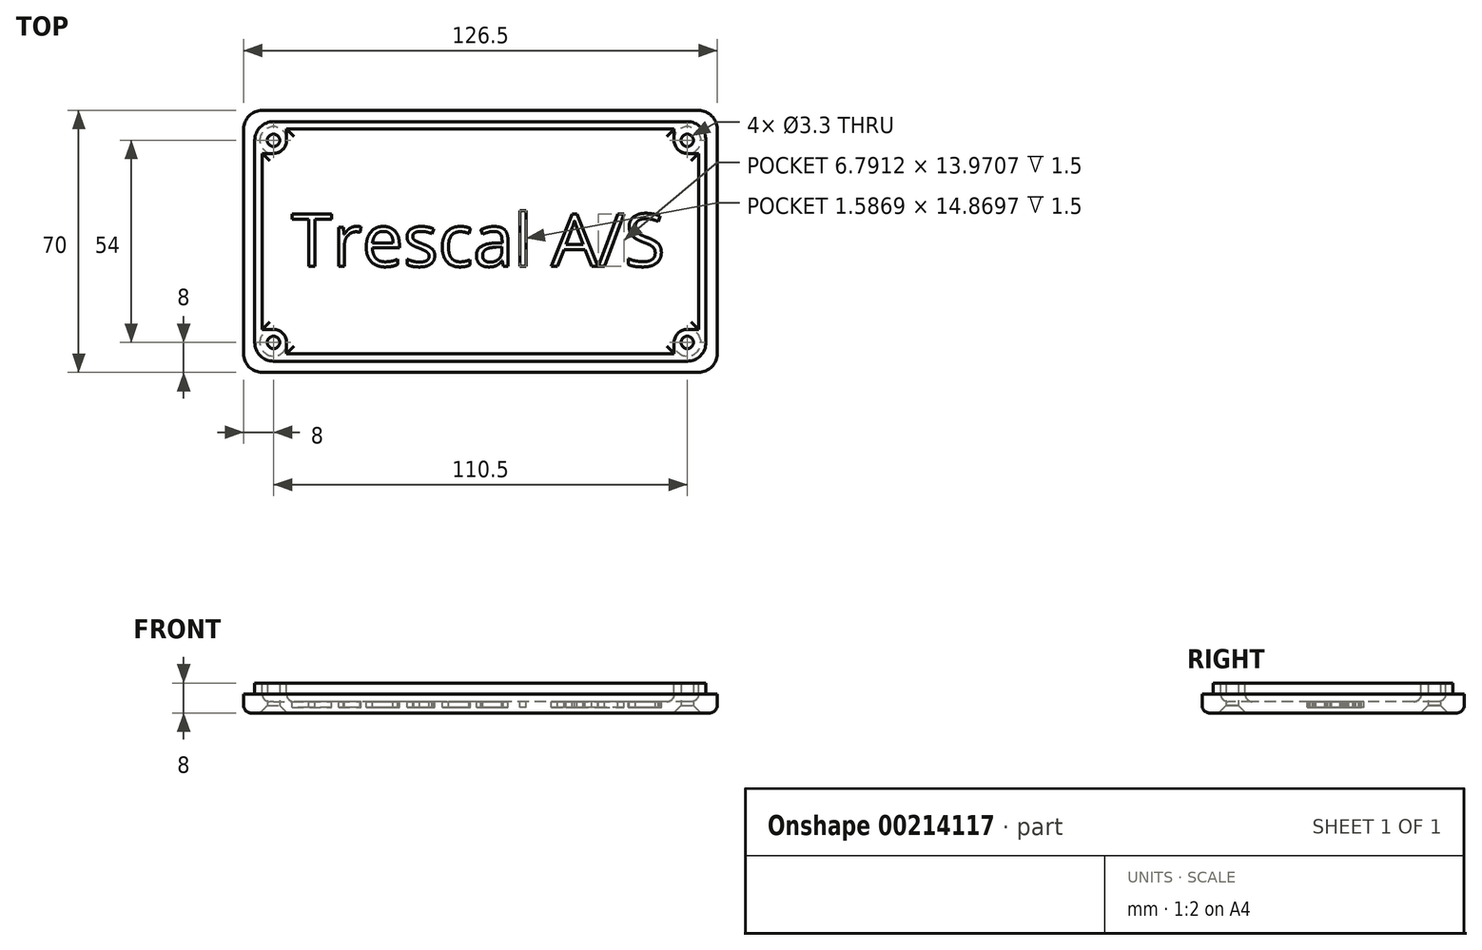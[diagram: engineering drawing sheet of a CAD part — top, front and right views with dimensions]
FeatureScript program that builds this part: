
annotation { "Feature Type Name" : "Feature", "Feature Type Description" : "" }
export const myFeature = defineFeature(function(context is Context, id is Id, definition is map)
    precondition{}
    {
        {
            var Q0;
            Q0=qCreatedBy(makeId("Top.planeOp"),FACE);
            var sketch = newSketch(context, id + "F0", { "sketchPlane" : qUnion([Q0])});
            skLineSegment(sketch, "E0.bottom", {"start": v(58.25, -35) * mm, "end": v(-58.25, -35) * mm});
            skLineSegment(sketch, "E0.top", {"start": v(58.25, 35) * mm, "end": v(-58.25, 35) * mm});
            skLineSegment(sketch, "E0.left", {"start": v(63.25, -30) * mm, "end": v(63.25, 30) * mm});
            skLineSegment(sketch, "E0.right", {"start": v(-63.25, -30) * mm, "end": v(-63.25, 30) * mm});
            skPoint(sketch, "E0.middle", {"position": v(0, 0) * mm});
            skPoint(sketch, "E1.visualSharp", {"position": v(-63.25, 35) * mm});
            skArc(sketch, "E1.filletArc", {"start": v(-58.25, 35) * mm, "mid": v(-61.79, 33.54) * mm, "end": v(-63.25, 30) * mm});
            skPoint(sketch, "E2.visualSharp", {"position": v(63.25, 35) * mm});
            skArc(sketch, "E2.filletArc", {"start": v(63.25, 30) * mm, "mid": v(61.79, 33.54) * mm, "end": v(58.25, 35) * mm});
            skPoint(sketch, "E3.visualSharp", {"position": v(63.25, -35) * mm});
            skArc(sketch, "E3.filletArc", {"start": v(58.25, -35) * mm, "mid": v(61.79, -33.54) * mm, "end": v(63.25, -30) * mm});
            skPoint(sketch, "E4.visualSharp", {"position": v(-63.25, -35) * mm});
            skArc(sketch, "E4.filletArc", {"start": v(-63.25, -30) * mm, "mid": v(-61.79, -33.54) * mm, "end": v(-58.25, -35) * mm});
            skLineSegment(sketch, "E5.bottom", {"start": v(55.25, -32) * mm, "end": v(-55.25, -32) * mm});
            skLineSegment(sketch, "E5.top", {"start": v(55.25, 32) * mm, "end": v(-55.25, 32) * mm});
            skLineSegment(sketch, "E5.left", {"start": v(60.25, -27) * mm, "end": v(60.25, 27) * mm});
            skLineSegment(sketch, "E5.right", {"start": v(-60.25, -27) * mm, "end": v(-60.25, 27) * mm});
            skPoint(sketch, "E6.visualSharp", {"position": v(-60.25, 32) * mm});
            skArc(sketch, "E6.filletArc", {"start": v(-55.25, 32) * mm, "mid": v(-58.79, 30.54) * mm, "end": v(-60.25, 27) * mm});
            skPoint(sketch, "E7.visualSharp", {"position": v(60.25, 32) * mm});
            skArc(sketch, "E7.filletArc", {"start": v(60.25, 27) * mm, "mid": v(58.79, 30.54) * mm, "end": v(55.25, 32) * mm});
            skPoint(sketch, "E8.visualSharp", {"position": v(60.25, -32) * mm});
            skArc(sketch, "E8.filletArc", {"start": v(55.25, -32) * mm, "mid": v(58.79, -30.54) * mm, "end": v(60.25, -27) * mm});
            skPoint(sketch, "E9.visualSharp", {"position": v(-60.25, -32) * mm});
            skArc(sketch, "E9.filletArc", {"start": v(-60.25, -27) * mm, "mid": v(-58.79, -30.54) * mm, "end": v(-55.25, -32) * mm});
            skSolve(sketch);
        }
        {
            var Q0;
            Q0=makeQuery(id+"F0.imprint","IMPRINT",FACE,{"disambiguationData":[TD([[makeQuery(id+"F0.imprint","IMPRINT",EDGE,{"derivedFrom":sQuery(id+"F0.wireOp",EDGE,"E5.bottom")}),-1.0]])]});
            extrude(context, id + "F1", {"entities" : qUnion([Q0]), "depth" : 8 * mm});
        }
        {
            var Q0;
            Q0 = qSketchRegion(id + "F0", true);
            extrude(context, id + "F2", {"entities" : qUnion([Q0]), "operationType" : NewBodyOperationType.ADD, "depth" : 5 * mm});
        }
        {
            var Q0;
            Q0=sQuery(id+"F0.wireOp",VERTEX,"E9.filletArc.center");
            var Q1;
            Q1=sQuery(id+"F0.wireOp",VERTEX,"E8.filletArc.center");
            var Q2;
            Q2=sQuery(id+"F0.wireOp",VERTEX,"E7.filletArc.center");
            var Q3;
            Q3=sQuery(id+"F0.wireOp",VERTEX,"E6.filletArc.center");
            var Q4;
            Q4=makeQuery(id+"F1.opExtrude","SWEPT_BODY",BODY,{"disambiguationData":[OSD([sQuery(id+"F0.wireOp",EDGE,"E5.bottom"),sQuery(id+"F0.wireOp",EDGE,"E5.top"),sQuery(id+"F0.wireOp",EDGE,"E5.left"),sQuery(id+"F0.wireOp",EDGE,"E5.right"),sQuery(id+"F0.wireOp",EDGE,"E6.filletArc"),sQuery(id+"F0.wireOp",EDGE,"E7.filletArc"),sQuery(id+"F0.wireOp",EDGE,"E8.filletArc"),sQuery(id+"F0.wireOp",EDGE,"E9.filletArc")])]});
            hole(context, id + "F3", {"style" : HoleStyle.C_SINK, "endStyle" : HoleEndStyle.THROUGH, "oppositeDirection" : true, "holeDiameter" : 3.3 * mm, "cSinkDiameter" : 7.3 * mm, "cSinkAngle" : 90 * degree, "locations" : qUnion([Q0, Q1, Q2, Q3]), "scope" : qUnion([Q4]), "isTappedThrough" : true});
        }
        {
            var Q0;
            Q0=makeQuery(id+"F1.opExtrude","CAP_FACE",FACE,{"disambiguationData":[OSD([sQuery(id+"F0.wireOp",EDGE,"E5.bottom"),sQuery(id+"F0.wireOp",EDGE,"E5.top"),sQuery(id+"F0.wireOp",EDGE,"E5.left"),sQuery(id+"F0.wireOp",EDGE,"E5.right"),sQuery(id+"F0.wireOp",EDGE,"E6.filletArc"),sQuery(id+"F0.wireOp",EDGE,"E7.filletArc"),sQuery(id+"F0.wireOp",EDGE,"E8.filletArc"),sQuery(id+"F0.wireOp",EDGE,"E9.filletArc")])],"isStart":false});
            var sketch = newSketch(context, id + "F4", { "sketchPlane" : qUnion([Q0])});
            skLineSegment(sketch, "E10.bottom", {"start": v(58.25, 23.5) * mm, "end": v(-58.25, 23.5) * mm});
            skLineSegment(sketch, "E10.top", {"start": v(58.25, -23.5) * mm, "end": v(-58.25, -23.5) * mm});
            skLineSegment(sketch, "E10.left", {"start": v(58.25, 23.5) * mm, "end": v(58.25, -23.5) * mm});
            skLineSegment(sketch, "E10.right", {"start": v(-58.25, 23.5) * mm, "end": v(-58.25, -23.5) * mm});
            skPoint(sketch, "E10.middle", {"position": v(0, 0) * mm});
            skLineSegment(sketch, "E11.bottom", {"start": v(51.75, 30) * mm, "end": v(-51.75, 30) * mm});
            skLineSegment(sketch, "E11.top", {"start": v(51.75, -30) * mm, "end": v(-51.75, -30) * mm});
            skLineSegment(sketch, "E11.left", {"start": v(51.75, 30) * mm, "end": v(51.75, -30) * mm});
            skLineSegment(sketch, "E11.right", {"start": v(-51.75, 30) * mm, "end": v(-51.75, -30) * mm});
            skSolve(sketch);
        }
        {
            var Q0;
            Q0 = qSketchRegion(id + "F4", true);
            extrude(context, id + "F5", {"entities" : qUnion([Q0]), "operationType" : NewBodyOperationType.REMOVE, "oppositeDirection" : true, "depth" : 5 * mm});
        }
        {
            var Q0;
            Q0=makeQuery(id+"F5.boolean.opBoolean","COPY",EDGE,{"derivedFrom":makeQuery(id+"F5.opExtrude","SWEPT_EDGE",EDGE,{"disambiguationData":[OSD([sQuery(id+"F4.wireOp",EDGE,"E10.bottom"),sQuery(id+"F4.wireOp",EDGE,"E11.left")])]})});
            var Q1;
            Q1=makeQuery(id+"F5.boolean.opBoolean","COPY",EDGE,{"derivedFrom":makeQuery(id+"F5.opExtrude","SWEPT_EDGE",EDGE,{"disambiguationData":[OSD([sQuery(id+"F4.wireOp",EDGE,"E10.top"),sQuery(id+"F4.wireOp",EDGE,"E11.left")])]})});
            var Q2;
            Q2=makeQuery(id+"F5.boolean.opBoolean","COPY",EDGE,{"derivedFrom":makeQuery(id+"F5.opExtrude","SWEPT_EDGE",EDGE,{"disambiguationData":[OSD([sQuery(id+"F4.wireOp",EDGE,"E10.top"),sQuery(id+"F4.wireOp",EDGE,"E11.right")])]})});
            var Q3;
            Q3=makeQuery(id+"F5.boolean.opBoolean","COPY",EDGE,{"derivedFrom":makeQuery(id+"F5.opExtrude","SWEPT_EDGE",EDGE,{"disambiguationData":[OSD([sQuery(id+"F4.wireOp",EDGE,"E10.bottom"),sQuery(id+"F4.wireOp",EDGE,"E11.right")])]})});
            fillet(context, id + "F6", {"entities" : qUnion([Q0, Q1, Q2, Q3]), "radius" : 3.5 * mm, "tangentPropagation" : true, "allowEdgeOverflow" : false});
        }
        {
            var Q0;
            Q0=makeQuery(id+"F2.opExtrude","CAP_EDGE",EDGE,{"disambiguationData":[OSD([sQuery(id+"F0.wireOp",EDGE,"E4.filletArc")])],"isStart":true});
            fillet(context, id + "F7", {"entities" : qUnion([Q0]), "radius" : 2 * mm, "tangentPropagation" : true, "allowEdgeOverflow" : false});
        }
        {
            var Q0;
            Q0=makeQuery(id+"F5.boolean.opBoolean","COPY",FACE,{"derivedFrom":makeQuery(id+"F5.opExtrude","CAP_FACE",FACE,{"disambiguationData":[OSD([sQuery(id+"F4.wireOp",EDGE,"E10.bottom"),sQuery(id+"F4.wireOp",EDGE,"E10.top"),sQuery(id+"F4.wireOp",EDGE,"E10.left"),sQuery(id+"F4.wireOp",EDGE,"E10.right"),sQuery(id+"F4.wireOp",EDGE,"E11.bottom"),sQuery(id+"F4.wireOp",EDGE,"E11.top"),sQuery(id+"F4.wireOp",EDGE,"E11.left"),sQuery(id+"F4.wireOp",EDGE,"E11.right")])],"isStart":false})});
            var sketch = newSketch(context, id + "F8", { "sketchPlane" : qUnion([Q0])});
            skText(sketch, "E12", { "text": "Trescal A/S", "fontName": "OpenSans-Regular.ttf"});
            const initialGuessF8  = {"E12": [-0.0504, -0.00665, 1, 0, 0.01409]};
            skSetInitialGuess(sketch, initialGuessF8);
            skSolve(sketch);
        }
        {
            var Q0;
            Q0 = qSketchRegion(id + "F8", true);
            extrude(context, id + "F9", {"entities" : qUnion([Q0]), "operationType" : NewBodyOperationType.REMOVE, "oppositeDirection" : true, "depth" : 1.5 * mm});
        }
        {
            var Q0;
            Q0=makeQuery(id+"F5.boolean.opBoolean","COPY",EDGE,{"derivedFrom":makeQuery(id+"F5.opExtrude","CAP_EDGE",EDGE,{"disambiguationData":[OSD([sQuery(id+"F4.wireOp",EDGE,"E11.bottom")])],"isStart":false})});
            var Q1;
            {var subQ0=sQuery(id+"F4.wireOp",EDGE,"E11.right");var subQ1=sQuery(id+"F4.wireOp",EDGE,"E10.bottom");Q1=makeQuery(id+"F6.opFillet","BLEND_EDGE",EDGE,{"blendedFrom":[makeQuery(id+"F5.boolean.opBoolean","COPY",EDGE,{"derivedFrom":makeQuery(id+"F5.opExtrude","SWEPT_EDGE",EDGE,{"disambiguationData":[OSD([subQ1,subQ0])]})}),makeQuery(id+"F5.boolean.opBoolean","COPY",FACE,{"derivedFrom":makeQuery(id+"F5.opExtrude","CAP_FACE",FACE,{"disambiguationData":[OSD([subQ1,sQuery(id+"F4.wireOp",EDGE,"E10.top"),sQuery(id+"F4.wireOp",EDGE,"E10.left"),sQuery(id+"F4.wireOp",EDGE,"E10.right"),sQuery(id+"F4.wireOp",EDGE,"E11.bottom"),sQuery(id+"F4.wireOp",EDGE,"E11.top"),sQuery(id+"F4.wireOp",EDGE,"E11.left"),subQ0])],"isStart":false})})],"blendedInto":[makeQuery(id+"F5.boolean.opBoolean","COPY",FACE,{"derivedFrom":makeQuery(id+"F5.opExtrude","CAP_FACE",FACE,{"disambiguationData":[OSD([subQ1,sQuery(id+"F4.wireOp",EDGE,"E10.top"),sQuery(id+"F4.wireOp",EDGE,"E10.left"),sQuery(id+"F4.wireOp",EDGE,"E10.right"),sQuery(id+"F4.wireOp",EDGE,"E11.bottom"),sQuery(id+"F4.wireOp",EDGE,"E11.top"),sQuery(id+"F4.wireOp",EDGE,"E11.left"),subQ0])],"isStart":false})})]});}
            var Q2;
            Q2=makeQuery(id+"F5.boolean.opBoolean","COPY",EDGE,{"derivedFrom":makeQuery(id+"F5.opExtrude","CAP_EDGE",EDGE,{"disambiguationData":[OSD([sQuery(id+"F4.wireOp",EDGE,"E10.right")])],"isStart":false})});
            var Q3;
            {var subQ0=sQuery(id+"F4.wireOp",EDGE,"E11.left");var subQ1=sQuery(id+"F4.wireOp",EDGE,"E10.bottom");Q3=makeQuery(id+"F6.opFillet","BLEND_EDGE",EDGE,{"blendedFrom":[makeQuery(id+"F5.boolean.opBoolean","COPY",EDGE,{"derivedFrom":makeQuery(id+"F5.opExtrude","SWEPT_EDGE",EDGE,{"disambiguationData":[OSD([subQ1,subQ0])]})}),makeQuery(id+"F5.boolean.opBoolean","COPY",FACE,{"derivedFrom":makeQuery(id+"F5.opExtrude","CAP_FACE",FACE,{"disambiguationData":[OSD([subQ1,sQuery(id+"F4.wireOp",EDGE,"E10.top"),sQuery(id+"F4.wireOp",EDGE,"E10.left"),sQuery(id+"F4.wireOp",EDGE,"E10.right"),sQuery(id+"F4.wireOp",EDGE,"E11.bottom"),sQuery(id+"F4.wireOp",EDGE,"E11.top"),subQ0,sQuery(id+"F4.wireOp",EDGE,"E11.right")])],"isStart":false})})],"blendedInto":[makeQuery(id+"F5.boolean.opBoolean","COPY",FACE,{"derivedFrom":makeQuery(id+"F5.opExtrude","CAP_FACE",FACE,{"disambiguationData":[OSD([subQ1,sQuery(id+"F4.wireOp",EDGE,"E10.top"),sQuery(id+"F4.wireOp",EDGE,"E10.left"),sQuery(id+"F4.wireOp",EDGE,"E10.right"),sQuery(id+"F4.wireOp",EDGE,"E11.bottom"),sQuery(id+"F4.wireOp",EDGE,"E11.top"),subQ0,sQuery(id+"F4.wireOp",EDGE,"E11.right")])],"isStart":false})})]});}
            var Q4;
            {var subQ0=sQuery(id+"F4.wireOp",EDGE,"E11.right");var subQ1=sQuery(id+"F4.wireOp",EDGE,"E10.top");Q4=makeQuery(id+"F6.opFillet","BLEND_EDGE",EDGE,{"blendedFrom":[makeQuery(id+"F5.boolean.opBoolean","COPY",EDGE,{"derivedFrom":makeQuery(id+"F5.opExtrude","SWEPT_EDGE",EDGE,{"disambiguationData":[OSD([subQ1,subQ0])]})}),makeQuery(id+"F5.boolean.opBoolean","COPY",FACE,{"derivedFrom":makeQuery(id+"F5.opExtrude","CAP_FACE",FACE,{"disambiguationData":[OSD([sQuery(id+"F4.wireOp",EDGE,"E10.bottom"),subQ1,sQuery(id+"F4.wireOp",EDGE,"E10.left"),sQuery(id+"F4.wireOp",EDGE,"E10.right"),sQuery(id+"F4.wireOp",EDGE,"E11.bottom"),sQuery(id+"F4.wireOp",EDGE,"E11.top"),sQuery(id+"F4.wireOp",EDGE,"E11.left"),subQ0])],"isStart":false})})],"blendedInto":[makeQuery(id+"F5.boolean.opBoolean","COPY",FACE,{"derivedFrom":makeQuery(id+"F5.opExtrude","CAP_FACE",FACE,{"disambiguationData":[OSD([sQuery(id+"F4.wireOp",EDGE,"E10.bottom"),subQ1,sQuery(id+"F4.wireOp",EDGE,"E10.left"),sQuery(id+"F4.wireOp",EDGE,"E10.right"),sQuery(id+"F4.wireOp",EDGE,"E11.bottom"),sQuery(id+"F4.wireOp",EDGE,"E11.top"),sQuery(id+"F4.wireOp",EDGE,"E11.left"),subQ0])],"isStart":false})})]});}
            var Q5;
            Q5=makeQuery(id+"F5.boolean.opBoolean","COPY",EDGE,{"derivedFrom":makeQuery(id+"F5.opExtrude","CAP_EDGE",EDGE,{"disambiguationData":[OSD([sQuery(id+"F4.wireOp",EDGE,"E11.top")])],"isStart":false})});
            var Q6;
            {var subQ0=sQuery(id+"F4.wireOp",EDGE,"E11.left");var subQ1=sQuery(id+"F4.wireOp",EDGE,"E10.top");Q6=makeQuery(id+"F6.opFillet","BLEND_EDGE",EDGE,{"blendedFrom":[makeQuery(id+"F5.boolean.opBoolean","COPY",EDGE,{"derivedFrom":makeQuery(id+"F5.opExtrude","SWEPT_EDGE",EDGE,{"disambiguationData":[OSD([subQ1,subQ0])]})}),makeQuery(id+"F5.boolean.opBoolean","COPY",FACE,{"derivedFrom":makeQuery(id+"F5.opExtrude","CAP_FACE",FACE,{"disambiguationData":[OSD([sQuery(id+"F4.wireOp",EDGE,"E10.bottom"),subQ1,sQuery(id+"F4.wireOp",EDGE,"E10.left"),sQuery(id+"F4.wireOp",EDGE,"E10.right"),sQuery(id+"F4.wireOp",EDGE,"E11.bottom"),sQuery(id+"F4.wireOp",EDGE,"E11.top"),subQ0,sQuery(id+"F4.wireOp",EDGE,"E11.right")])],"isStart":false})})],"blendedInto":[makeQuery(id+"F5.boolean.opBoolean","COPY",FACE,{"derivedFrom":makeQuery(id+"F5.opExtrude","CAP_FACE",FACE,{"disambiguationData":[OSD([sQuery(id+"F4.wireOp",EDGE,"E10.bottom"),subQ1,sQuery(id+"F4.wireOp",EDGE,"E10.left"),sQuery(id+"F4.wireOp",EDGE,"E10.right"),sQuery(id+"F4.wireOp",EDGE,"E11.bottom"),sQuery(id+"F4.wireOp",EDGE,"E11.top"),subQ0,sQuery(id+"F4.wireOp",EDGE,"E11.right")])],"isStart":false})})]});}
            var Q7;
            Q7=makeQuery(id+"F5.boolean.opBoolean","COPY",EDGE,{"derivedFrom":makeQuery(id+"F5.opExtrude","CAP_EDGE",EDGE,{"disambiguationData":[OSD([sQuery(id+"F4.wireOp",EDGE,"E10.left")])],"isStart":false})});
            fillet(context, id + "F10", {"entities" : qUnion([Q0, Q1, Q2, Q3, Q4, Q5, Q6, Q7]), "radius" : 2 * mm, "tangentPropagation" : true, "allowEdgeOverflow" : false});
        }
    });
